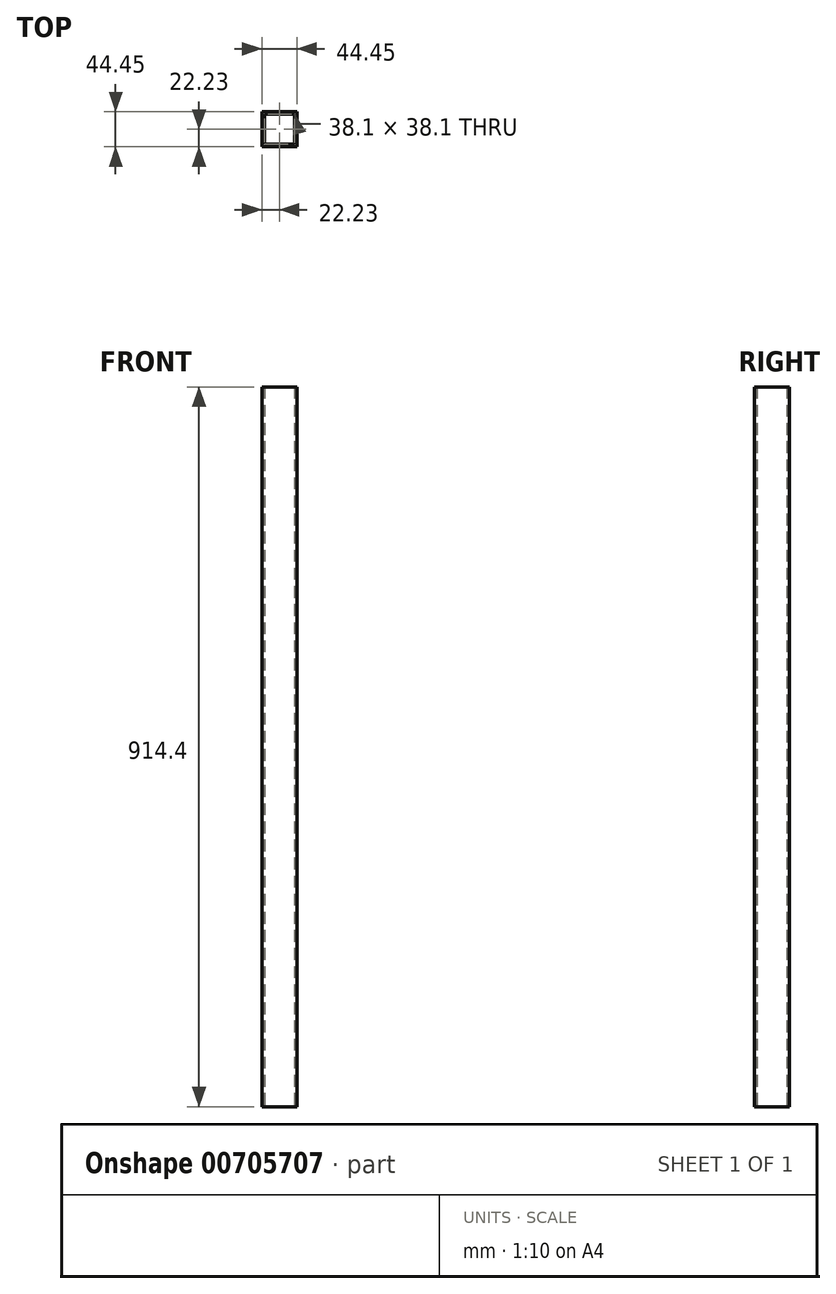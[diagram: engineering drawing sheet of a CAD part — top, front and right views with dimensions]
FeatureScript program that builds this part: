
annotation { "Feature Type Name" : "Feature", "Feature Type Description" : "" }
export const myFeature = defineFeature(function(context is Context, id is Id, definition is map)
    precondition{}
    {
        {
            var Q0;
            Q0=qCreatedBy(makeId("Top.planeOp"),FACE);
            var sketch = newSketch(context, id + "F0", { "sketchPlane" : qUnion([Q0])});
            skLineSegment(sketch, "E0.bottom", {"start": v(0, 0) * mm, "end": v(38.1, 0) * mm});
            skLineSegment(sketch, "E0.top", {"start": v(0, 38.1) * mm, "end": v(38.1, 38.1) * mm});
            skLineSegment(sketch, "E0.left", {"start": v(0, 0) * mm, "end": v(0, 38.1) * mm});
            skLineSegment(sketch, "E0.right", {"start": v(38.1, 0) * mm, "end": v(38.1, 38.1) * mm});
            skLineSegment(sketch, "E1.0", {"start": v(-3.18, 41.27) * mm, "end": v(41.27, 41.27) * mm});
            skLineSegment(sketch, "E1.1", {"start": v(-3.17, -3.17) * mm, "end": v(-3.18, 41.27) * mm});
            skLineSegment(sketch, "E1.2", {"start": v(-3.17, -3.17) * mm, "end": v(41.28, -3.17) * mm});
            skLineSegment(sketch, "E1.3", {"start": v(41.28, -3.17) * mm, "end": v(41.27, 41.27) * mm});
            skSolve(sketch);
        }
        {
            var Q0;
            Q0 = qSketchRegion(id + "F0", true);
            extrude(context, id + "F1", {"entities" : qUnion([Q0]), "depth" : 914.4 * mm, "offsetDistance" : 25.4 * mm});
        }
    });
